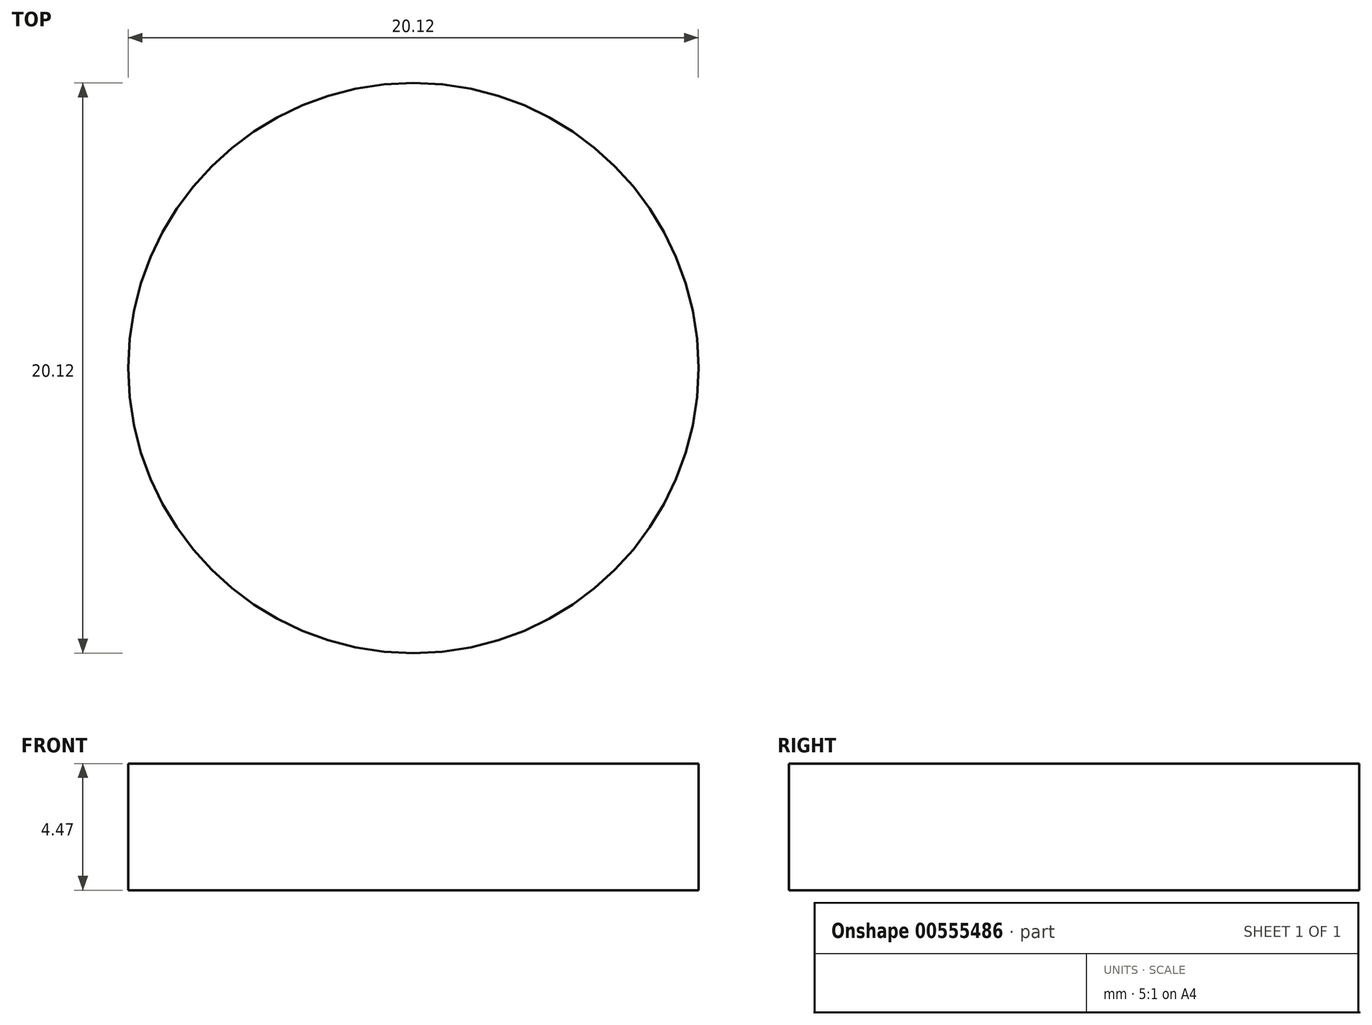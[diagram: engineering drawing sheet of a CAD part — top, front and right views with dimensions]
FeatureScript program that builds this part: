
annotation { "Feature Type Name" : "Feature", "Feature Type Description" : "" }
export const myFeature = defineFeature(function(context is Context, id is Id, definition is map)
    precondition{}
    {
        {
            var Q0;
            Q0=qCreatedBy(makeId("Top.planeOp"),FACE);
            var sketch = newSketch(context, id + "F0", { "sketchPlane" : qUnion([Q0])});
            skCircle(sketch, "E0", {"center": v(0, 0) * mm, "radius": 10.06 * mm});
            skSolve(sketch);
        }
        {
            var Q0;
            Q0=makeQuery(id+"F0.imprint","IMPRINT",FACE,{"disambiguationData":[TD([[makeQuery(id+"F0.imprint","IMPRINT",EDGE,{"derivedFrom":sQuery(id+"F0.wireOp",EDGE,"E0")}),1.0]])]});
            extrude(context, id + "F1", {"entities" : qUnion([Q0]), "depth" : 4.47 * mm, "offsetDistance" : 25.4 * mm});
        }
    });
